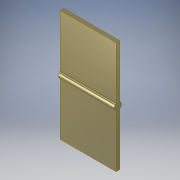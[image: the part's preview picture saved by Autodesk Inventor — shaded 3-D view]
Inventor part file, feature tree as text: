
AUTODESK INVENTOR PART (.ipt)
format: ipt  version: 2018 (Build 220112000, 112)  size: 103,424 bytes
history: native  units: in
note: dims shown in document units (in); Inventor stores cm internally (conversion verified against a paired STEP export)
features: extrude x1, sketch x1
ambient origin geometry x8: Origin, YZ Plane, XZ Plane, XY Plane, X Axis, Y Axis, Z Axis, Center Point
bodies: Solid1 (feature_tree)
feature tree (2):
  extrude  "Extrusion1"  Depth=0.0787in
  sketch  "Sketch1"  dims[d0=0.1575in d1=0.0787in d2=0.0394in d3=1.1811in d4=0.0in d26=1.1811in d27=1.1811in]
